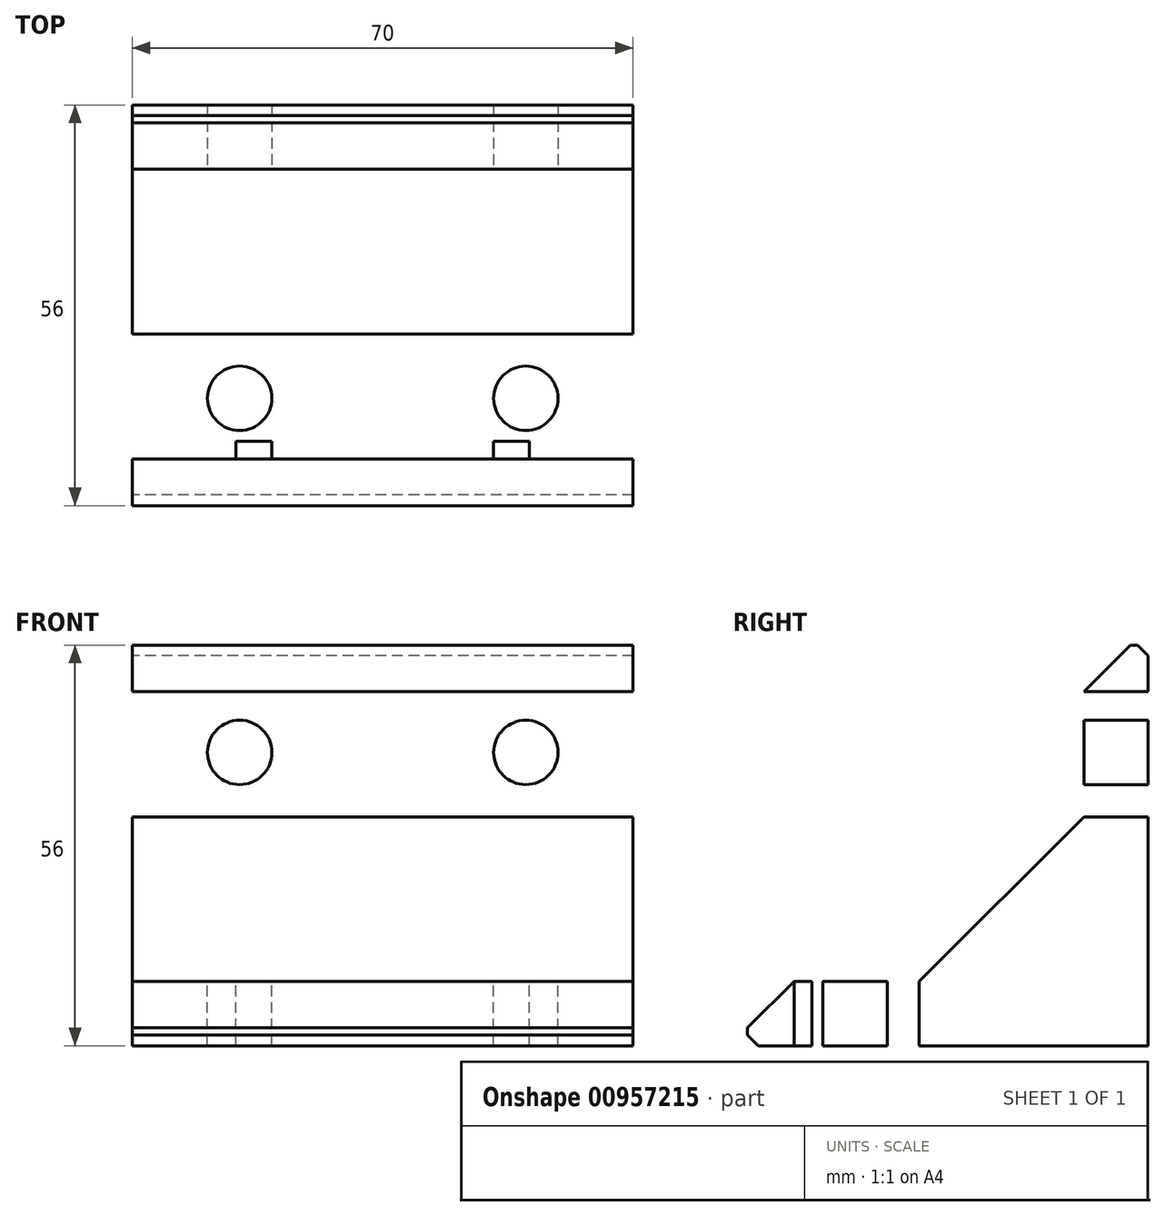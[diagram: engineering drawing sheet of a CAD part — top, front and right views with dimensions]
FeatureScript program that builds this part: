
annotation { "Feature Type Name" : "Feature", "Feature Type Description" : "" }
export const myFeature = defineFeature(function(context is Context, id is Id, definition is map)
    precondition{}
    {
        {
            var Q0;
            Q0=qCreatedBy(makeId("Right.planeOp"),FACE);
            var sketch = newSketch(context, id + "F0", { "sketchPlane" : qUnion([Q0])});
            skLineSegment(sketch, "E0", {"start": v(21.87, 1.4) * mm, "end": v(30.87, 1.4) * mm, "construction": true});
            skLineSegment(sketch, "E1", {"start": v(30.87, 10.4) * mm, "end": v(21.87, 10.4) * mm, "construction": true});
            skLineSegment(sketch, "E2", {"start": v(-14.63, -26.1) * mm, "end": v(-14.63, -35.1) * mm, "construction": true});
            skLineSegment(sketch, "E3", {"start": v(-5.63, -35.1) * mm, "end": v(-5.63, -26.1) * mm, "construction": true});
            skLineSegment(sketch, "E4", {"start": v(31.32, 5.9) * mm, "end": v(21.42, 5.9) * mm, "construction": true});
            skLineSegment(sketch, "E5", {"start": v(-10.13, -35.55) * mm, "end": v(-10.13, -25.65) * mm, "construction": true});
            skLineSegment(sketch, "E6", {"start": v(31.67, 11.9) * mm, "end": v(31.67, 17.9) * mm, "construction": true});
            skLineSegment(sketch, "E7", {"start": v(31.67, 17.9) * mm, "end": v(30.87, 17.9) * mm, "construction": true});
            skLineSegment(sketch, "E8", {"start": v(31.67, 11.9) * mm, "end": v(30.87, 11.9) * mm, "construction": true});
            skLineSegment(sketch, "E9", {"start": v(-22.13, -35.9) * mm, "end": v(-16.13, -35.9) * mm, "construction": true});
            skLineSegment(sketch, "E10", {"start": v(-22.13, -35.9) * mm, "end": v(-22.13, -35.1) * mm, "construction": true});
            skLineSegment(sketch, "E11", {"start": v(-16.13, -35.9) * mm, "end": v(-16.13, -35.1) * mm, "construction": true});
            skLineSegment(sketch, "E12", {"start": v(-18.63, -26.1) * mm, "end": v(-25.13, -32.6) * mm});
            skLineSegment(sketch, "E13", {"start": v(-25.13, -32.6) * mm, "end": v(-25.13, -33.6) * mm});
            skLineSegment(sketch, "E14", {"start": v(-25.13, -33.6) * mm, "end": v(-23.63, -35.1) * mm});
            skLineSegment(sketch, "E15", {"start": v(-23.63, -35.1) * mm, "end": v(30.87, -35.1) * mm});
            skLineSegment(sketch, "E16", {"start": v(30.87, -35.1) * mm, "end": v(30.87, 19.4) * mm});
            skLineSegment(sketch, "E17", {"start": v(30.87, 19.4) * mm, "end": v(29.37, 20.9) * mm});
            skLineSegment(sketch, "E18", {"start": v(29.37, 20.9) * mm, "end": v(28.37, 20.9) * mm});
            skLineSegment(sketch, "E19", {"start": v(28.37, 20.9) * mm, "end": v(21.87, 14.4) * mm});
            skLineSegment(sketch, "E20", {"start": v(21.87, 14.4) * mm, "end": v(21.87, -3.1) * mm});
            skLineSegment(sketch, "E21", {"start": v(21.87, -3.1) * mm, "end": v(-1.13, -26.1) * mm});
            skLineSegment(sketch, "E22", {"start": v(-1.13, -26.1) * mm, "end": v(-18.63, -26.1) * mm});
            skSolve(sketch);
        }
        {
            var Q0;
            Q0=makeQuery(id+"F0.imprint","IMPRINT",FACE,{"disambiguationData":[TD([[makeQuery(id+"F0.imprint","IMPRINT",EDGE,{"derivedFrom":sQuery(id+"F0.wireOp",EDGE,"E12")}),1.0]])]});
            extrude(context, id + "F1", {"entities" : qUnion([Q0]), "endBound" : BoundingType.SYMMETRIC, "depth" : 70 * mm, "offsetDistance" : 25 * mm});
        }
        {
            var Q0;
            Q0=qCreatedBy(makeId("Front.planeOp"),FACE);
            var sketch = newSketch(context, id + "F2", { "sketchPlane" : qUnion([Q0])});
            skLineSegment(sketch, "E23", {"start": v(-15.5, 11.9) * mm, "end": v(-15.5, 17.9) * mm, "construction": true});
            skLineSegment(sketch, "E24", {"start": v(-20.5, 11.9) * mm, "end": v(-15.5, 11.9) * mm, "construction": true});
            skLineSegment(sketch, "E25", {"start": v(-20.5, 17.9) * mm, "end": v(-20.5, 11.9) * mm, "construction": true});
            skLineSegment(sketch, "E26", {"start": v(-15.5, 17.9) * mm, "end": v(-20.5, 17.9) * mm, "construction": true});
            skLineSegment(sketch, "E27", {"start": v(20.5, 17.9) * mm, "end": v(15.5, 17.9) * mm, "construction": true});
            skLineSegment(sketch, "E28", {"start": v(20.5, 11.9) * mm, "end": v(20.5, 17.9) * mm, "construction": true});
            skLineSegment(sketch, "E29", {"start": v(15.5, 11.9) * mm, "end": v(20.5, 11.9) * mm, "construction": true});
            skLineSegment(sketch, "E30", {"start": v(15.5, 17.9) * mm, "end": v(15.5, 11.9) * mm, "construction": true});
            skLineSegment(sketch, "E31", {"start": v(35, 19.4) * mm, "end": v(-35, 19.4) * mm});
            skLineSegment(sketch, "E32", {"start": v(-24.5, -26.1) * mm, "end": v(-24.5, -35.1) * mm, "construction": true});
            skLineSegment(sketch, "E33", {"start": v(-15.5, -35.1) * mm, "end": v(-15.5, -26.1) * mm, "construction": true});
            skLineSegment(sketch, "E34", {"start": v(15.5, -26.1) * mm, "end": v(15.5, -35.1) * mm, "construction": true});
            skLineSegment(sketch, "E35", {"start": v(24.5, -35.1) * mm, "end": v(24.5, -26.1) * mm, "construction": true});
            skLineSegment(sketch, "E36", {"start": v(-24.72, 5.9) * mm, "end": v(-15.27, 5.9) * mm, "construction": true});
            skLineSegment(sketch, "E37", {"start": v(-20, 1.17) * mm, "end": v(-20, 10.62) * mm, "construction": true});
            skLineSegment(sketch, "E38", {"start": v(15.28, 5.9) * mm, "end": v(24.73, 5.9) * mm, "construction": true});
            skLineSegment(sketch, "E39", {"start": v(20, 1.17) * mm, "end": v(20, 10.62) * mm, "construction": true});
            skLineSegment(sketch, "E40", {"start": v(20, -35.55) * mm, "end": v(20, -25.65) * mm, "construction": true});
            skLineSegment(sketch, "E41", {"start": v(-20, -35.55) * mm, "end": v(-20, -25.65) * mm, "construction": true});
            skLineSegment(sketch, "E42", {"start": v(35, 20.9) * mm, "end": v(-35, 20.9) * mm});
            skCircle(sketch, "E43", {"center": v(-20, 5.9) * mm, "radius": 4.5 * mm});
            skCircle(sketch, "E44", {"center": v(20, 5.9) * mm, "radius": 4.5 * mm});
            skLineSegment(sketch, "E45", {"start": v(35, 14.4) * mm, "end": v(-35, 14.4) * mm});
            skLineSegment(sketch, "E46", {"start": v(35, -3.1) * mm, "end": v(-35, -3.1) * mm});
            skLineSegment(sketch, "E47", {"start": v(15.5, -35.9) * mm, "end": v(15.5, -35.1) * mm, "construction": true});
            skLineSegment(sketch, "E48", {"start": v(15.5, -35.9) * mm, "end": v(20.5, -35.9) * mm, "construction": true});
            skLineSegment(sketch, "E49", {"start": v(20.5, -35.9) * mm, "end": v(20.5, -35.1) * mm, "construction": true});
            skLineSegment(sketch, "E50", {"start": v(-20.5, -35.9) * mm, "end": v(-20.5, -35.1) * mm, "construction": true});
            skLineSegment(sketch, "E51", {"start": v(-20.5, -35.9) * mm, "end": v(-15.5, -35.9) * mm, "construction": true});
            skLineSegment(sketch, "E52", {"start": v(-15.5, -35.9) * mm, "end": v(-15.5, -35.1) * mm, "construction": true});
            skLineSegment(sketch, "E53", {"start": v(35, -35.1) * mm, "end": v(-35, -35.1) * mm});
            skLineSegment(sketch, "E54", {"start": v(35, -33.6) * mm, "end": v(-35, -33.6) * mm});
            skLineSegment(sketch, "E55", {"start": v(-35, 20.9) * mm, "end": v(-35, -35.1) * mm});
            skLineSegment(sketch, "E56", {"start": v(35, -32.6) * mm, "end": v(-35, -32.6) * mm});
            skLineSegment(sketch, "E57", {"start": v(35, 20.9) * mm, "end": v(35, -35.1) * mm});
            skLineSegment(sketch, "E58", {"start": v(35, -26.1) * mm, "end": v(-35, -26.1) * mm});
            skSolve(sketch);
        }
        {
            var Q0;
            Q0=makeQuery(id+"F2.imprint","IMPRINT",FACE,{"disambiguationData":[TD([[makeQuery(id+"F2.imprint","IMPRINT",EDGE,{"derivedFrom":sQuery(id+"F2.wireOp",EDGE,"E43")}),-1.0]])]});
            var Q1;
            Q1=makeQuery(id+"F2.imprint","IMPRINT",FACE,{"disambiguationData":[TD([[makeQuery(id+"F2.imprint","IMPRINT",EDGE,{"derivedFrom":sQuery(id+"F2.wireOp",EDGE,"E44")}),-1.0]])]});
            extrude(context, id + "F3", {"entities" : qUnion([Q0, Q1]), "operationType" : NewBodyOperationType.REMOVE, "endBound" : BoundingType.THROUGH_ALL, "oppositeDirection" : true, "depth" : 25 * mm, "offsetDistance" : 25 * mm});
        }
        {
            var Q0;
            Q0=qCreatedBy(makeId("Top.planeOp"),FACE);
            var sketch = newSketch(context, id + "F4", { "sketchPlane" : qUnion([Q0])});
            skLineSegment(sketch, "E59", {"start": v(20.5, -16.13) * mm, "end": v(15.5, -16.13) * mm});
            skLineSegment(sketch, "E60", {"start": v(-15.5, -16.13) * mm, "end": v(-20.5, -16.13) * mm});
            skLineSegment(sketch, "E61", {"start": v(15.5, -16.13) * mm, "end": v(15.5, -22.13) * mm});
            skLineSegment(sketch, "E62", {"start": v(-20.5, -22.13) * mm, "end": v(-15.5, -22.13) * mm});
            skLineSegment(sketch, "E63", {"start": v(-20.5, -16.13) * mm, "end": v(-20.5, -22.13) * mm});
            skLineSegment(sketch, "E64", {"start": v(20.5, -22.13) * mm, "end": v(20.5, -16.13) * mm});
            skLineSegment(sketch, "E65", {"start": v(15.5, -22.13) * mm, "end": v(20.5, -22.13) * mm});
            skLineSegment(sketch, "E66", {"start": v(-15.5, -22.13) * mm, "end": v(-15.5, -16.13) * mm});
            skLineSegment(sketch, "E67", {"start": v(35, -23.63) * mm, "end": v(-35, -23.63) * mm});
            skLineSegment(sketch, "E68", {"start": v(-15.5, 21.87) * mm, "end": v(-15.5, 30.87) * mm});
            skLineSegment(sketch, "E69", {"start": v(-24.5, 30.87) * mm, "end": v(-24.5, 21.87) * mm});
            skLineSegment(sketch, "E70", {"start": v(24.5, 21.87) * mm, "end": v(24.5, 30.87) * mm});
            skLineSegment(sketch, "E71", {"start": v(15.5, 30.87) * mm, "end": v(15.5, 21.87) * mm});
            skLineSegment(sketch, "E72", {"start": v(15.28, -10.13) * mm, "end": v(24.73, -10.13) * mm, "construction": true});
            skLineSegment(sketch, "E73", {"start": v(20, -14.85) * mm, "end": v(20, -5.4) * mm, "construction": true});
            skLineSegment(sketch, "E74", {"start": v(-24.72, -10.13) * mm, "end": v(-15.27, -10.13) * mm, "construction": true});
            skLineSegment(sketch, "E75", {"start": v(-20, -14.85) * mm, "end": v(-20, -5.4) * mm, "construction": true});
            skLineSegment(sketch, "E76", {"start": v(20, 31.32) * mm, "end": v(20, 21.42) * mm});
            skLineSegment(sketch, "E77", {"start": v(-20, 31.32) * mm, "end": v(-20, 21.42) * mm});
            skLineSegment(sketch, "E78", {"start": v(35, -25.13) * mm, "end": v(-35, -25.13) * mm});
            skCircle(sketch, "E79", {"center": v(20, -10.13) * mm, "radius": 4.5 * mm});
            skCircle(sketch, "E80", {"center": v(-20, -10.13) * mm, "radius": 4.5 * mm});
            skLineSegment(sketch, "E81", {"start": v(35, -18.63) * mm, "end": v(-35, -18.63) * mm});
            skLineSegment(sketch, "E82", {"start": v(35, -1.13) * mm, "end": v(-35, -1.13) * mm});
            skLineSegment(sketch, "E83", {"start": v(15.5, 31.67) * mm, "end": v(15.5, 30.87) * mm});
            skLineSegment(sketch, "E84", {"start": v(20.5, 31.67) * mm, "end": v(15.5, 31.67) * mm});
            skLineSegment(sketch, "E85", {"start": v(20.5, 31.67) * mm, "end": v(20.5, 30.87) * mm});
            skLineSegment(sketch, "E86", {"start": v(-15.5, 31.67) * mm, "end": v(-20.5, 31.67) * mm});
            skLineSegment(sketch, "E87", {"start": v(-15.5, 31.67) * mm, "end": v(-15.5, 30.87) * mm});
            skLineSegment(sketch, "E88", {"start": v(-20.5, 31.67) * mm, "end": v(-20.5, 30.87) * mm});
            skLineSegment(sketch, "E89", {"start": v(35, 21.87) * mm, "end": v(-35, 21.87) * mm});
            skLineSegment(sketch, "E90", {"start": v(35, 28.37) * mm, "end": v(-35, 28.37) * mm});
            skLineSegment(sketch, "E91", {"start": v(35, 30.87) * mm, "end": v(35, -25.13) * mm});
            skLineSegment(sketch, "E92", {"start": v(-35, 30.87) * mm, "end": v(-35, -25.13) * mm});
            skLineSegment(sketch, "E93", {"start": v(35, 29.37) * mm, "end": v(-35, 29.37) * mm});
            skLineSegment(sketch, "E94", {"start": v(35, 30.87) * mm, "end": v(-35, 30.87) * mm});
            skSolve(sketch);
        }
        {
            var Q0;
            Q0=makeQuery(id+"F4.imprint","IMPRINT",FACE,{"disambiguationData":[TD([[makeQuery(id+"F4.imprint","IMPRINT",EDGE,{"derivedFrom":sQuery(id+"F4.wireOp",EDGE,"E80")}),-1.0]])]});
            var Q1;
            Q1=makeQuery(id+"F4.imprint","IMPRINT",FACE,{"disambiguationData":[TD([[makeQuery(id+"F4.imprint","IMPRINT",EDGE,{"derivedFrom":sQuery(id+"F4.wireOp",EDGE,"E79")}),-1.0]])]});
            var Q2;
            Q2=sQuery(id+"F4.wireOp",EDGE,"E80");
            var Q3;
            Q3=sQuery(id+"F4.wireOp",EDGE,"E79");
            extrude(context, id + "F5", {"entities" : qUnion([Q0, Q1]), "operationType" : NewBodyOperationType.REMOVE, "surfaceEntities" : qUnion([Q2, Q3]), "endBound" : BoundingType.THROUGH_ALL, "oppositeDirection" : true, "depth" : 25 * mm, "offsetDistance" : 25 * mm});
        }
    });
